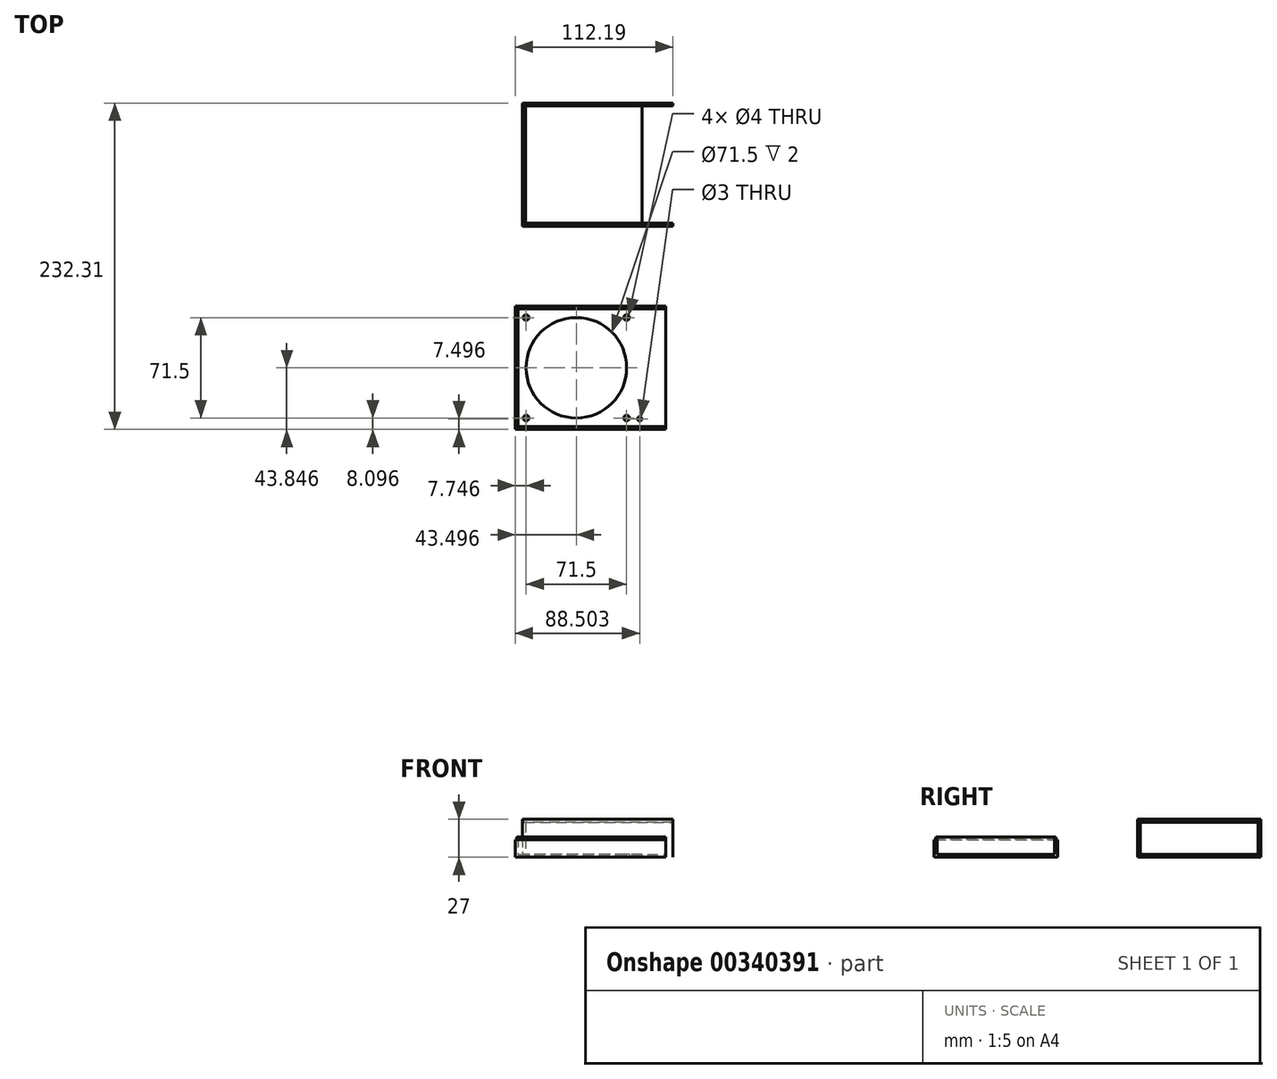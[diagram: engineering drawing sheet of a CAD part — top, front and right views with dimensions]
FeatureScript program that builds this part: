
annotation { "Feature Type Name" : "Feature", "Feature Type Description" : "" }
export const myFeature = defineFeature(function(context is Context, id is Id, definition is map)
    precondition{}
    {
        {
            var Q0;
            Q0=qCreatedBy(makeId("Top.planeOp"),FACE);
            var sketch = newSketch(context, id + "F0", { "sketchPlane" : qUnion([Q0])});
            skLineSegment(sketch, "E0.bottom", {"start": v(41.5, -41.85) * mm, "end": v(-41.5, -41.85) * mm});
            skLineSegment(sketch, "E0.top", {"start": v(41.5, 41.85) * mm, "end": v(-41.5, 41.85) * mm});
            skLineSegment(sketch, "E0.left", {"start": v(41.5, -41.85) * mm, "end": v(41.5, 41.85) * mm});
            skLineSegment(sketch, "E0.right", {"start": v(-41.5, -41.85) * mm, "end": v(-41.5, 41.85) * mm});
            skPoint(sketch, "E0.middle", {"position": v(0, 0) * mm});
            skLineSegment(sketch, "E1", {"start": v(41.5, -41.85) * mm, "end": v(63.5, -41.85) * mm});
            skLineSegment(sketch, "E2", {"start": v(63.5, -41.85) * mm, "end": v(63.5, -43.85) * mm});
            skLineSegment(sketch, "E3", {"start": v(63.5, -43.85) * mm, "end": v(-43.5, -43.85) * mm});
            skLineSegment(sketch, "E4", {"start": v(-43.5, -43.85) * mm, "end": v(-43.5, 43.85) * mm});
            skLineSegment(sketch, "E5", {"start": v(41.5, 41.85) * mm, "end": v(63.5, 41.85) * mm});
            skLineSegment(sketch, "E6", {"start": v(63.5, 41.85) * mm, "end": v(63.5, 43.85) * mm});
            skLineSegment(sketch, "E7", {"start": v(63.5, 43.85) * mm, "end": v(-43.5, 43.85) * mm});
            skSolve(sketch);
        }
        {
            var Q0;
            Q0=makeQuery(id+"F0.imprint","IMPRINT",FACE,{"disambiguationData":[TD([[makeQuery(id+"F0.imprint","IMPRINT",EDGE,{"derivedFrom":sQuery(id+"F0.wireOp",EDGE,"E0.bottom")}),1.0]])]});
            extrude(context, id + "F1", {"entities" : qUnion([Q0]), "depth" : 25 * mm});
        }
        {
            var Q0;
            Q0=makeQuery(id+"F0.imprint","IMPRINT",FACE,{"disambiguationData":[TD([[makeQuery(id+"F0.imprint","IMPRINT",EDGE,{"derivedFrom":sQuery(id+"F0.wireOp",EDGE,"E0.bottom")}),-1.0]])]});
            extrude(context, id + "F2", {"entities" : qUnion([Q0]), "operationType" : NewBodyOperationType.ADD, "depth" : 2 * mm});
        }
        {
            var Q0;
            Q0=qCreatedBy(makeId("Top.planeOp"),FACE);
            var sketch = newSketch(context, id + "F3", { "sketchPlane" : qUnion([Q0])});
            skLineSegment(sketch, "E8.bottom", {"start": v(-48.7, -100.76) * mm, "end": v(58.3, -100.76) * mm});
            skLineSegment(sketch, "E8.top", {"start": v(-48.7, -188.46) * mm, "end": v(58.3, -188.46) * mm});
            skLineSegment(sketch, "E8.left", {"start": v(-48.7, -100.76) * mm, "end": v(-48.7, -188.46) * mm});
            skLineSegment(sketch, "E9.right", {"start": v(-40.94, -108.86) * mm, "end": v(-40.94, -105.89) * mm, "construction": true});
            skCircle(sketch, "E10", {"center": v(-40.94, -108.86) * mm, "radius": 2 * mm});
            skCircle(sketch, "E11", {"center": v(30.56, -108.86) * mm, "radius": 2 * mm});
            skCircle(sketch, "E12", {"center": v(30.56, -180.36) * mm, "radius": 2 * mm});
            skCircle(sketch, "E13", {"center": v(-40.94, -180.36) * mm, "radius": 2 * mm});
            skCircle(sketch, "E14", {"center": v(-5.2, -144.61) * mm, "radius": 35.75 * mm});
            skCircle(sketch, "E15", {"center": v(39.81, -180.96) * mm, "radius": 1.5 * mm});
            skLineSegment(sketch, "E16", {"start": v(58.3, -188.46) * mm, "end": v(58.3, -186.46) * mm});
            skLineSegment(sketch, "E17", {"start": v(58.3, -100.76) * mm, "end": v(58.3, -102.76) * mm});
            skLineSegment(sketch, "E18", {"start": v(-46.7, -186.46) * mm, "end": v(-46.7, -102.76) * mm});
            skLineSegment(sketch, "E19", {"start": v(-46.7, -186.46) * mm, "end": v(58.3, -186.46) * mm});
            skLineSegment(sketch, "E20", {"start": v(58.3, -102.76) * mm, "end": v(-46.7, -102.76) * mm});
            skLineSegment(sketch, "E21", {"start": v(58.3, -186.46) * mm, "end": v(58.3, -102.76) * mm});
            skSolve(sketch);
        }
        {
            var Q0;
            Q0=makeQuery(id+"F1.opExtrude","CAP_FACE",FACE,{"disambiguationData":[OSD([sQuery(id+"F0.wireOp",EDGE,"E0.bottom"),sQuery(id+"F0.wireOp",EDGE,"E0.top"),sQuery(id+"F0.wireOp",EDGE,"E0.right"),sQuery(id+"F0.wireOp",EDGE,"E1"),sQuery(id+"F0.wireOp",EDGE,"E2"),sQuery(id+"F0.wireOp",EDGE,"E3"),sQuery(id+"F0.wireOp",EDGE,"E4"),sQuery(id+"F0.wireOp",EDGE,"E5"),sQuery(id+"F0.wireOp",EDGE,"E6"),sQuery(id+"F0.wireOp",EDGE,"E7")])],"isStart":false});
            var sketch = newSketch(context, id + "F4", { "sketchPlane" : qUnion([Q0])});
            skLineSegment(sketch, "E22", {"start": v(-42.5, -42.85) * mm, "end": v(63.5, -42.85) * mm});
            skLineSegment(sketch, "E23", {"start": v(63.5, 42.85) * mm, "end": v(-42.5, 42.85) * mm});
            skLineSegment(sketch, "E24", {"start": v(-42.5, 42.85) * mm, "end": v(-42.5, -42.85) * mm});
            skLineSegment(sketch, "E25", {"start": v(63.5, -42.85) * mm, "end": v(63.5, -43.85) * mm});
            skLineSegment(sketch, "E26", {"start": v(-43.5, -43.85) * mm, "end": v(-43.5, 43.85) * mm});
            skLineSegment(sketch, "E27", {"start": v(-43.5, 43.85) * mm, "end": v(63.5, 43.85) * mm});
            skLineSegment(sketch, "E28", {"start": v(63.5, 43.85) * mm, "end": v(63.5, 42.85) * mm});
            skLineSegment(sketch, "E29", {"start": v(-43.5, -43.85) * mm, "end": v(63.5, -43.85) * mm});
            skSolve(sketch);
        }
        {
            var Q0;
            Q0 = qSketchRegion(id + "F4", true);
            extrude(context, id + "F5", {"entities" : qUnion([Q0]), "operationType" : NewBodyOperationType.ADD, "depth" : 2 * mm});
        }
        {
            var Q0;
            Q0=makeQuery(id+"F3.imprint","IMPRINT",FACE,{"disambiguationData":[TD([[makeQuery(id+"F3.imprint","IMPRINT",EDGE,{"derivedFrom":sQuery(id+"F3.wireOp",EDGE,"E8.bottom")}),-1.0]])]});
            extrude(context, id + "F6", {"entities" : qUnion([Q0]), "depth" : 2 * mm});
        }
        {
            var Q0;
            Q0=makeQuery(id+"F3.imprint","IMPRINT",FACE,{"disambiguationData":[TD([[makeQuery(id+"F3.imprint","IMPRINT",EDGE,{"derivedFrom":sQuery(id+"F3.wireOp",EDGE,"E8.bottom")}),-1.0]])]});
            extrude(context, id + "F7", {"entities" : qUnion([Q0]), "operationType" : NewBodyOperationType.ADD, "depth" : 12.5 * mm});
        }
        {
            var Q0;
            Q0=makeQuery(id+"F3.imprint","IMPRINT",FACE,{"disambiguationData":[TD([[makeQuery(id+"F3.imprint","IMPRINT",EDGE,{"derivedFrom":sQuery(id+"F3.wireOp",EDGE,"E10")}),-1.0]])]});
            extrude(context, id + "F8", {"entities" : qUnion([Q0]), "operationType" : NewBodyOperationType.ADD, "depth" : 2 * mm});
        }
        {
            var Q0;
            Q0=makeQuery(id+"F7.opExtrude","CAP_FACE",FACE,{"disambiguationData":[OSD([sQuery(id+"F3.wireOp",EDGE,"E8.bottom"),sQuery(id+"F3.wireOp",EDGE,"E8.top"),sQuery(id+"F3.wireOp",EDGE,"E8.left"),sQuery(id+"F3.wireOp",EDGE,"E16"),sQuery(id+"F3.wireOp",EDGE,"E17"),sQuery(id+"F3.wireOp",EDGE,"E18"),sQuery(id+"F3.wireOp",EDGE,"E19"),sQuery(id+"F3.wireOp",EDGE,"E20")])],"isStart":false});
            var sketch = newSketch(context, id + "F9", { "sketchPlane" : qUnion([Q0])});
            skLineSegment(sketch, "E30", {"start": v(58.3, -186.46) * mm, "end": v(58.3, -187.46) * mm});
            skLineSegment(sketch, "E31", {"start": v(58.3, -186.46) * mm, "end": v(-46.7, -186.46) * mm});
            skLineSegment(sketch, "E32", {"start": v(-46.7, -186.46) * mm, "end": v(-46.7, -102.76) * mm});
            skLineSegment(sketch, "E33", {"start": v(-46.7, -102.76) * mm, "end": v(58.3, -102.76) * mm});
            skLineSegment(sketch, "E34", {"start": v(58.3, -102.76) * mm, "end": v(58.3, -101.76) * mm});
            skLineSegment(sketch, "E35", {"start": v(-47.7, -187.46) * mm, "end": v(-47.7, -101.76) * mm});
            skLineSegment(sketch, "E36", {"start": v(-47.7, -187.46) * mm, "end": v(58.3, -187.46) * mm});
            skLineSegment(sketch, "E37", {"start": v(-47.7, -101.76) * mm, "end": v(58.3, -101.76) * mm});
            skSolve(sketch);
        }
        {
            var Q0;
            Q0=makeQuery(id+"F9.imprint","IMPRINT",FACE,{"disambiguationData":[TD([[makeQuery(id+"F9.imprint","IMPRINT",EDGE,{"derivedFrom":sQuery(id+"F9.wireOp",EDGE,"E30")}),1.0]])]});
            extrude(context, id + "F10", {"entities" : qUnion([Q0]), "operationType" : NewBodyOperationType.ADD, "depth" : 2 * mm});
        }
    });
